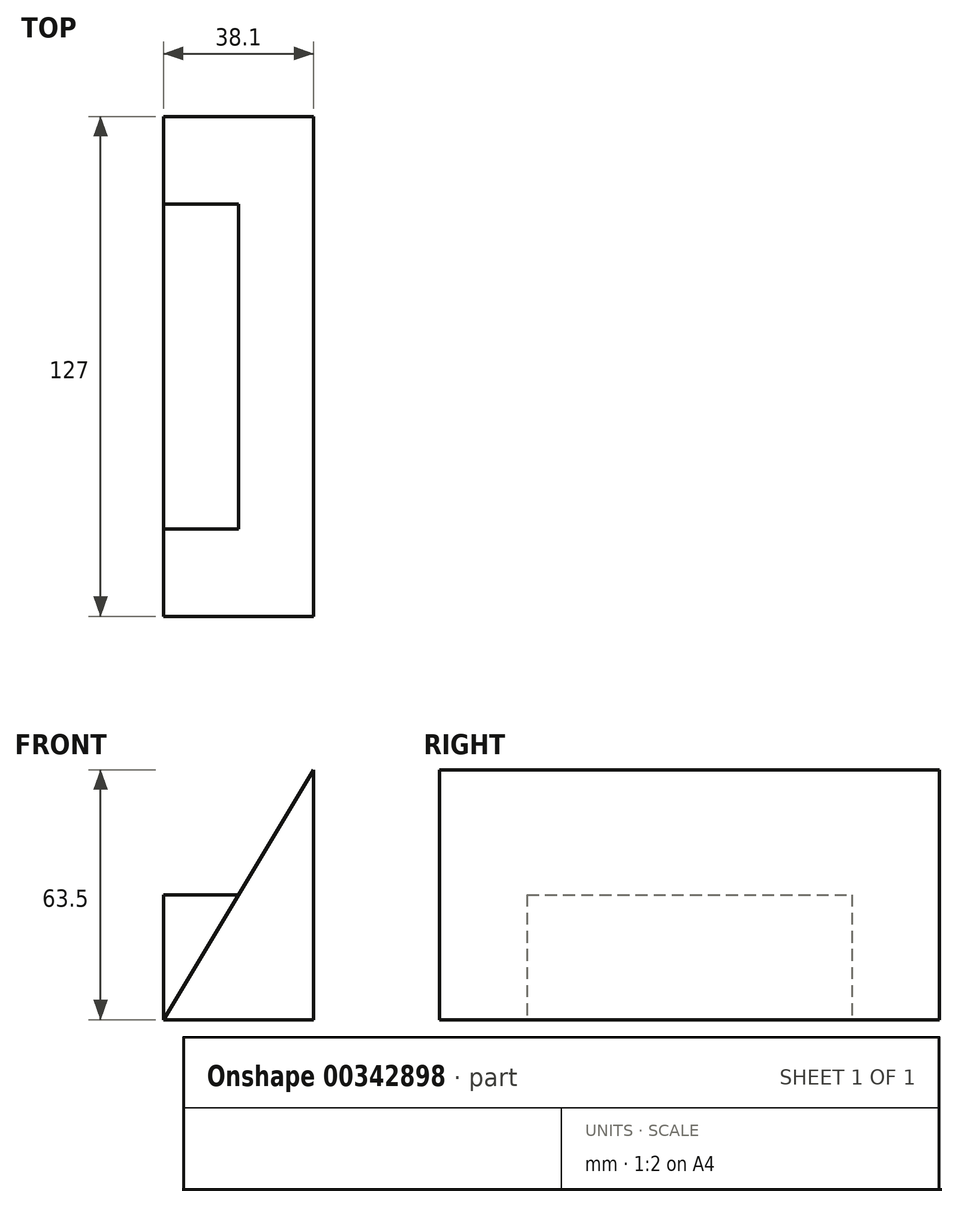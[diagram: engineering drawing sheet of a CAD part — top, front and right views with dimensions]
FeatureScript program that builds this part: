
annotation { "Feature Type Name" : "Feature", "Feature Type Description" : "" }
export const myFeature = defineFeature(function(context is Context, id is Id, definition is map)
    precondition{}
    {
        {
            var Q0;
            Q0=qCreatedBy(makeId("Front.planeOp"),FACE);
            var sketch = newSketch(context, id + "F0", { "sketchPlane" : qUnion([Q0])});
            skLineSegment(sketch, "E0.top", {"start": v(-44.89, -31.04) * mm, "end": v(-6.79, -31.04) * mm});
            skLineSegment(sketch, "E0.left", {"start": v(-44.89, 0.7) * mm, "end": v(-44.89, -31.04) * mm});
            skLineSegment(sketch, "E0.right", {"start": v(-6.79, 32.46) * mm, "end": v(-6.79, -31.04) * mm});
            skLineSegment(sketch, "E1", {"start": v(-44.89, -31.04) * mm, "end": v(-6.79, 32.46) * mm});
            skLineSegment(sketch, "E2", {"start": v(-44.89, 0) * mm, "end": v(-44.89, -31.04) * mm});
            skLineSegment(sketch, "E3", {"start": v(-25.84, 0.7) * mm, "end": v(-44.89, 0.7) * mm});
            skPoint(sketch, "E4.orphan", {"position": v(-44.89, 32.46) * mm});
            skSolve(sketch);
        }
        {
            var Q0;
            Q0=makeQuery(id+"F0.imprint","IMPRINT",FACE,{"disambiguationData":[TD([[makeQuery(id+"F0.imprint","IMPRINT",EDGE,{"derivedFrom":sQuery(id+"F0.wireOp",EDGE,"E0.top")}),1.0]])]});
            extrude(context, id + "F1", {"entities" : qUnion([Q0]), "depth" : 127 * mm});
        }
        {
            var Q0;
            {var subQ3=sQuery(id+"F0.wireOp",EDGE,"E3");Q0=makeQuery(id+"F0.imprint","IMPRINT",FACE,{"disambiguationData":[TD([[makeQuery(id+"F0.imprint","IMPRINT",EDGE,{"derivedFrom":subQ3}),1.0]])]});}
            extrude(context, id + "F2", {"entities" : qUnion([Q0]), "operationType" : NewBodyOperationType.ADD, "depth" : 127 * mm});
        }
        {
            var Q0;
            {var subQ0=sQuery(id+"F0.wireOp",EDGE,"E1");Q0=makeQuery(id+"F2.boolean.opBoolean","MERGE",FACE,{"derivedFrom":[makeQuery(id+"F1.opExtrude","CAP_FACE",FACE,{"disambiguationData":[OSD([sQuery(id+"F0.wireOp",EDGE,"E0.top"),sQuery(id+"F0.wireOp",EDGE,"E0.right"),subQ0])],"isStart":false}),makeQuery(id+"F2.opExtrude","CAP_FACE",FACE,{"disambiguationData":[OSD([subQ0,sQuery(id+"F0.wireOp",EDGE,"E3"),sQuery(id+"F0.wireOp",EDGE,"E0.left")])],"isStart":false})]});}
            var sketch = newSketch(context, id + "F3", { "sketchPlane" : qUnion([Q0])});
            skLineSegment(sketch, "E5", {"start": v(-44.89, -31.04) * mm, "end": v(-25.84, 0.7) * mm});
            skSolve(sketch);
        }
        {
            var Q0;
            Q0=makeQuery(id+"F3.imprint","IMPRINT",FACE,{"disambiguationData":[TD([[makeQuery(id+"F3.imprint","IMPRINT",EDGE,{"derivedFrom":sQuery(id+"F3.wireOp",EDGE,"E5")}),1.0]])]});
            extrude(context, id + "F4", {"entities" : qUnion([Q0]), "operationType" : NewBodyOperationType.REMOVE, "oppositeDirection" : true, "depth" : 22.22 * mm});
        }
        {
            var Q0;
            {var subQ3=sQuery(id+"F0.wireOp",EDGE,"E3");Q0=makeQuery(id+"F0.imprint","IMPRINT",FACE,{"disambiguationData":[TD([[makeQuery(id+"F0.imprint","IMPRINT",EDGE,{"derivedFrom":subQ3}),1.0]])]});}
            extrude(context, id + "F5", {"entities" : qUnion([Q0]), "operationType" : NewBodyOperationType.REMOVE, "depth" : 22.22 * mm});
        }
    });
